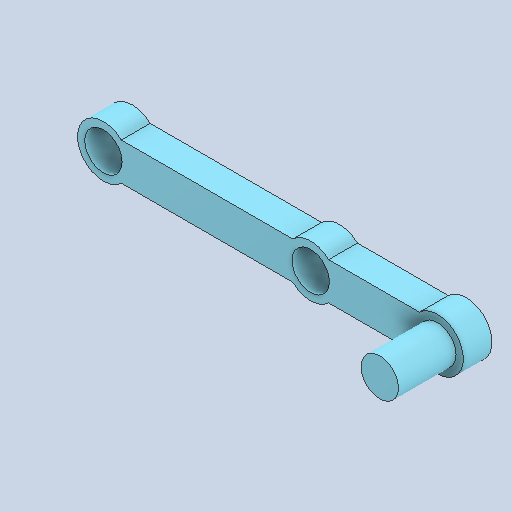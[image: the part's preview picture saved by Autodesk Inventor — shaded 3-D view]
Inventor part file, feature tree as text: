
AUTODESK INVENTOR PART (.ipt)
format: ipt  version: 2022 (Build 260153000, 153)  size: 131,584 bytes
history: native  units: in
note: dims shown in document units (in); Inventor stores cm internally (conversion verified against a paired STEP export)
features: other x3, sketch x1
ambient origin geometry x8: Origin, YZ Plane, XZ Plane, XY Plane, X Axis, Y Axis, Z Axis, Center Point
bodies: Solid1 (feature_tree)
feature tree (4):
  other  "Component38.ipt"
  other  "Solid1::Component38.ipt"
  other  "TaggingFeature1"
  sketch  "Sketch2"  dims[d0=0.3937in]
